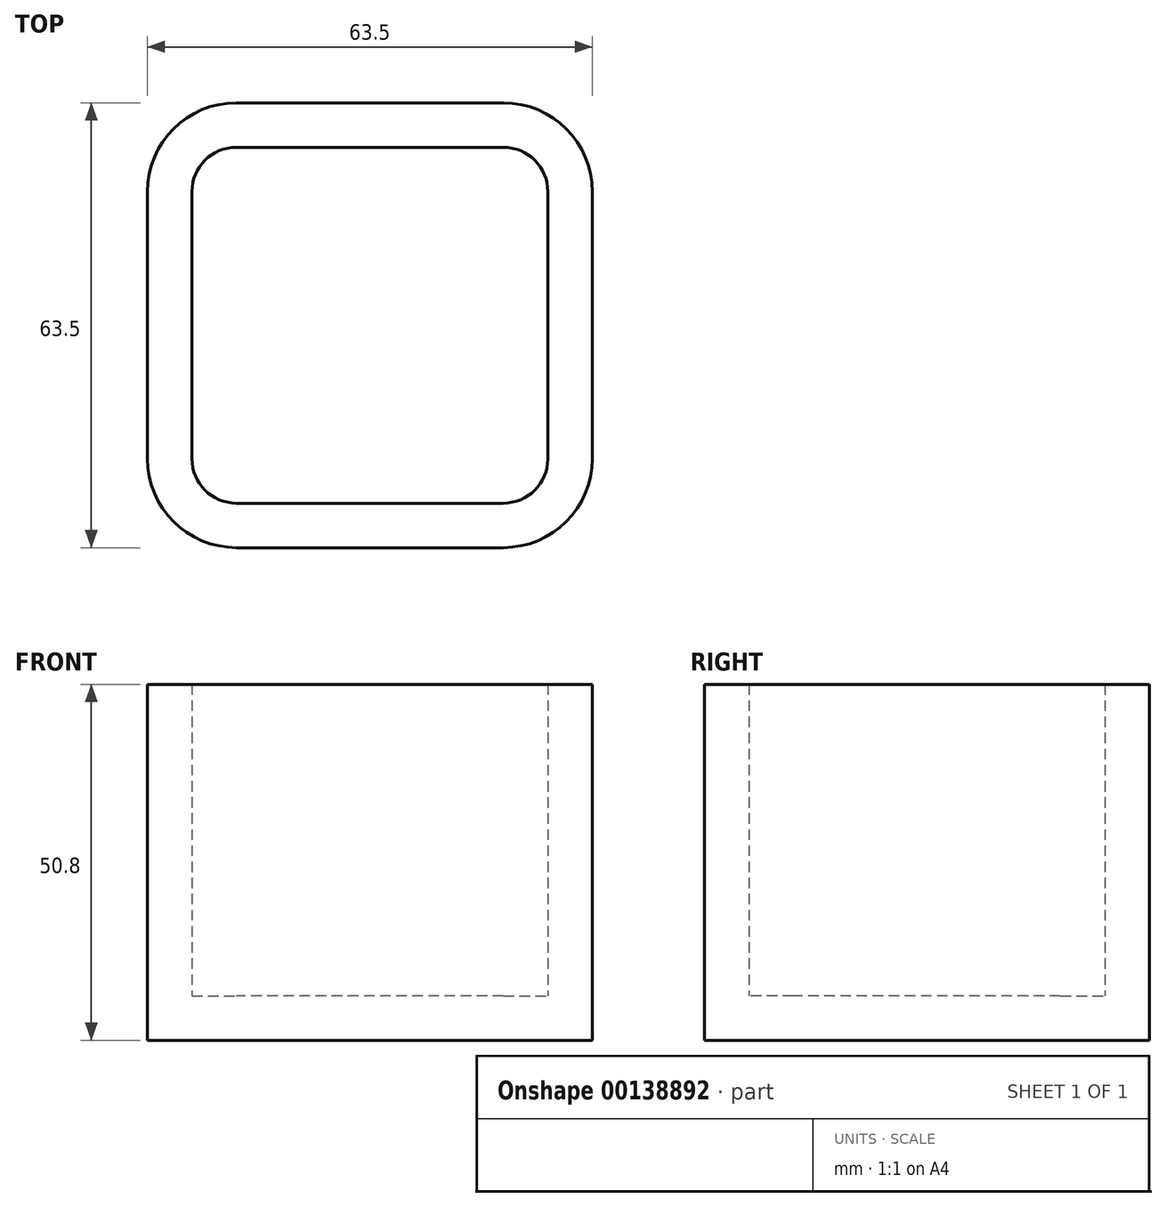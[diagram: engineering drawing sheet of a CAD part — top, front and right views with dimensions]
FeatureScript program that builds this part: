
annotation { "Feature Type Name" : "Feature", "Feature Type Description" : "" }
export const myFeature = defineFeature(function(context is Context, id is Id, definition is map)
    precondition{}
    {
        {
            var Q0;
            Q0=qCreatedBy(makeId("Top.planeOp"),FACE);
            var sketch = newSketch(context, id + "F0", { "sketchPlane" : qUnion([Q0])});
            skLineSegment(sketch, "E0.bottom", {"start": v(31.75, 31.75) * mm, "end": v(-31.75, 31.75) * mm});
            skLineSegment(sketch, "E0.top", {"start": v(31.75, -31.75) * mm, "end": v(-31.75, -31.75) * mm});
            skLineSegment(sketch, "E0.left", {"start": v(31.75, 31.75) * mm, "end": v(31.75, -31.75) * mm});
            skLineSegment(sketch, "E0.right", {"start": v(-31.75, 31.75) * mm, "end": v(-31.75, -31.75) * mm});
            skPoint(sketch, "E0.middle", {"position": v(0, 0) * mm});
            skSolve(sketch);
        }
        {
            var Q0;
            Q0 = qSketchRegion(id + "F0", true);
            extrude(context, id + "F1", {"entities" : qUnion([Q0]), "depth" : 50.8 * mm});
        }
        {
            var Q0;
            Q0=makeQuery(id+"F1.opExtrude","SWEPT_EDGE",EDGE,{"disambiguationData":[OSD([sQuery(id+"F0.wireOp",EDGE,"E0.top"),sQuery(id+"F0.wireOp",EDGE,"E0.right")])]});
            var Q1;
            Q1=makeQuery(id+"F1.opExtrude","SWEPT_EDGE",EDGE,{"disambiguationData":[OSD([sQuery(id+"F0.wireOp",EDGE,"E0.top"),sQuery(id+"F0.wireOp",EDGE,"E0.left")])]});
            var Q2;
            Q2=makeQuery(id+"F1.opExtrude","SWEPT_EDGE",EDGE,{"disambiguationData":[OSD([sQuery(id+"F0.wireOp",EDGE,"E0.bottom"),sQuery(id+"F0.wireOp",EDGE,"E0.left")])]});
            var Q3;
            Q3=makeQuery(id+"F1.opExtrude","SWEPT_EDGE",EDGE,{"disambiguationData":[OSD([sQuery(id+"F0.wireOp",EDGE,"E0.bottom"),sQuery(id+"F0.wireOp",EDGE,"E0.right")])]});
            fillet(context, id + "F2", {"entities" : qUnion([Q0, Q1, Q2, Q3]), "radius" : 12.7 * mm, "tangentPropagation" : true, "allowEdgeOverflow" : false});
        }
        {
            var Q0;
            Q0=makeQuery(id+"F1.opExtrude","CAP_FACE",FACE,{"disambiguationData":[OSD([sQuery(id+"F0.wireOp",EDGE,"E0.bottom"),sQuery(id+"F0.wireOp",EDGE,"E0.top"),sQuery(id+"F0.wireOp",EDGE,"E0.left"),sQuery(id+"F0.wireOp",EDGE,"E0.right")])],"isStart":false});
            shell(context, id + "F3", {"entities" : qUnion([Q0]), "thickness" : 6.35 * mm});
        }
    });
